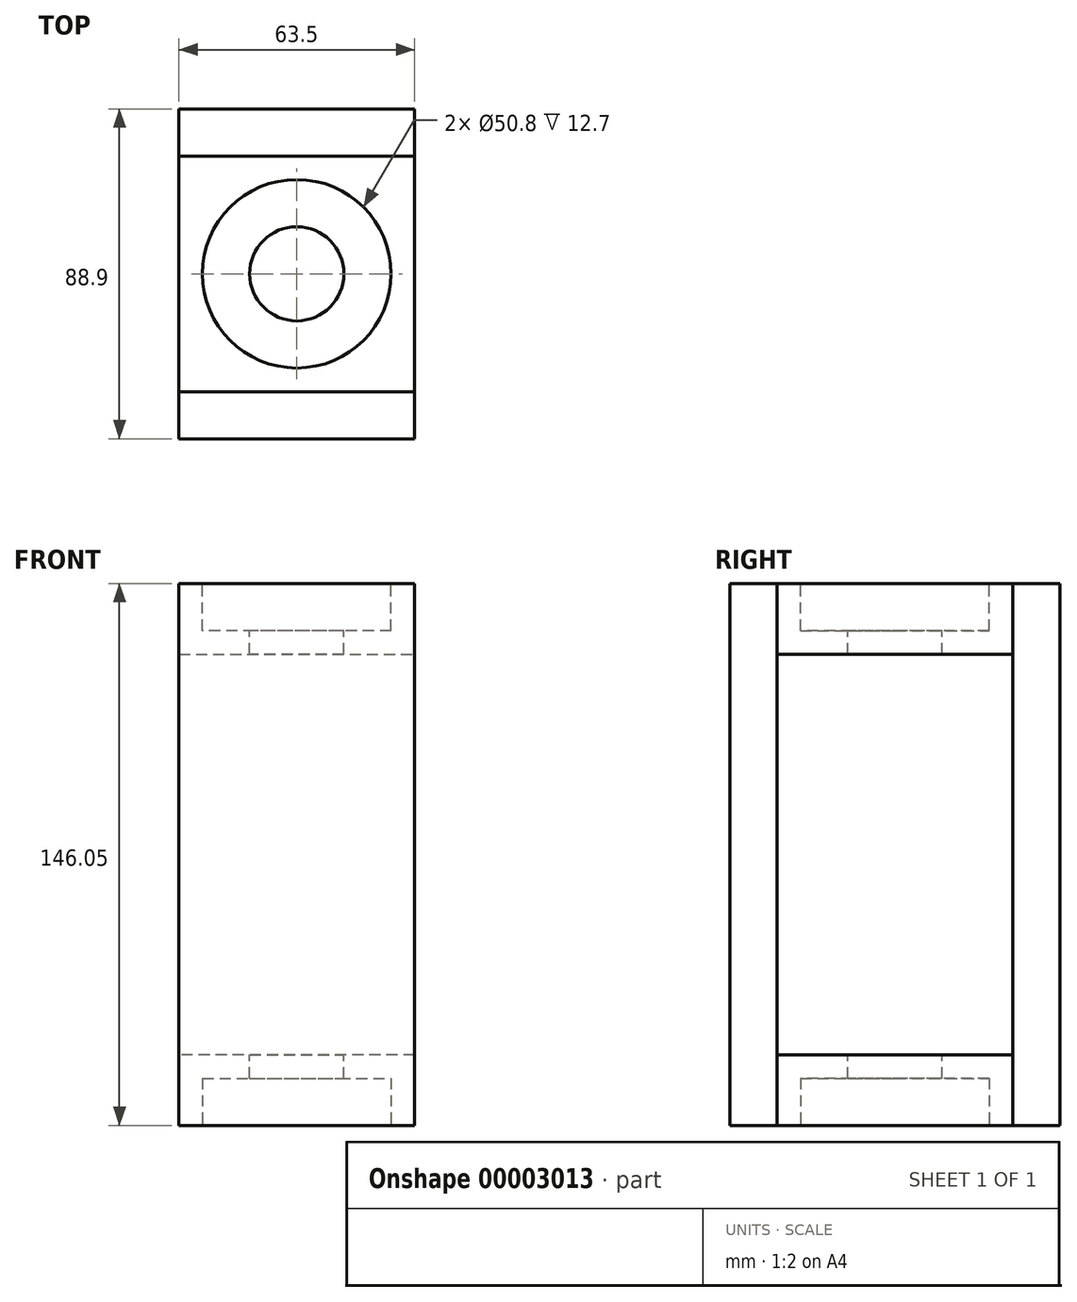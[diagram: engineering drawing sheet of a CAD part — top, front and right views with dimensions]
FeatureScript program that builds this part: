
annotation { "Feature Type Name" : "Feature", "Feature Type Description" : "" }
export const myFeature = defineFeature(function(context is Context, id is Id, definition is map)
    precondition{}
    {
        {
            var Q0;
            Q0=qCreatedBy(makeId("Top.planeOp"),FACE);
            var sketch = newSketch(context, id + "F0", { "sketchPlane" : qUnion([Q0])});
            skLineSegment(sketch, "E0.bottom", {"start": v(0, 0) * mm, "end": v(63.5, 0) * mm});
            skLineSegment(sketch, "E0.top", {"start": v(0, 63.5) * mm, "end": v(63.5, 63.5) * mm});
            skLineSegment(sketch, "E0.left", {"start": v(0, 0) * mm, "end": v(0, 63.5) * mm});
            skLineSegment(sketch, "E0.right", {"start": v(63.5, 0) * mm, "end": v(63.5, 63.5) * mm});
            skSolve(sketch);
        }
        {
            var Q0;
            Q0=makeQuery(id+"F0.imprint","IMPRINT",FACE,{"disambiguationData":[TD([[makeQuery(id+"F0.imprint","IMPRINT",EDGE,{"derivedFrom":sQuery(id+"F0.wireOp",EDGE,"E0.bottom")}),1.0]])]});
            extrude(context, id + "F1", {"entities" : qUnion([Q0]), "depth" : 19.05 * mm});
        }
        {
            var Q0;
            Q0=makeQuery(id+"F1.opExtrude","CAP_FACE",FACE,{"disambiguationData":[OSD([sQuery(id+"F0.wireOp",EDGE,"E0.bottom"),sQuery(id+"F0.wireOp",EDGE,"E0.top"),sQuery(id+"F0.wireOp",EDGE,"E0.left"),sQuery(id+"F0.wireOp",EDGE,"E0.right")])],"isStart":true});
            cPlane(context, id + "F2", {"entities" : qUnion([Q0]), "cplaneType" : CPlaneType.OFFSET, "offset" : 127 * mm, "width" : 152.4 * mm, "height" : 152.4 * mm});
        }
        {
            var Q0;
            Q0=qCreatedBy(id+"F2.planeOp",FACE);
            var sketch = newSketch(context, id + "F3", { "sketchPlane" : qUnion([Q0])});
            skLineSegment(sketch, "E1.0.0", {"start": v(0, 0) * mm, "end": v(0, -63.5) * mm});
            skLineSegment(sketch, "E1.0.1", {"start": v(0, -63.5) * mm, "end": v(63.5, -63.5) * mm});
            skLineSegment(sketch, "E1.0.2", {"start": v(63.5, -63.5) * mm, "end": v(63.5, 0) * mm});
            skLineSegment(sketch, "E1.0.3", {"start": v(63.5, 0) * mm, "end": v(0, 0) * mm});
            skSolve(sketch);
        }
        {
            var Q0;
            Q0=makeQuery(id+"F3.imprint","IMPRINT",FACE,{"disambiguationData":[TD([[makeQuery(id+"F3.imprint","IMPRINT",EDGE,{"derivedFrom":sQuery(id+"F3.wireOp",EDGE,"E1.0.0")}),1.0]])]});
            extrude(context, id + "F4", {"entities" : qUnion([Q0]), "oppositeDirection" : true, "depth" : 19.05 * mm});
        }
        {
            var Q0;
            Q0=makeQuery(id+"F1.opExtrude","CAP_FACE",FACE,{"disambiguationData":[OSD([sQuery(id+"F0.wireOp",EDGE,"E0.bottom"),sQuery(id+"F0.wireOp",EDGE,"E0.top"),sQuery(id+"F0.wireOp",EDGE,"E0.left"),sQuery(id+"F0.wireOp",EDGE,"E0.right")])],"isStart":false});
            var sketch = newSketch(context, id + "F5", { "sketchPlane" : qUnion([Q0])});
            skCircle(sketch, "E2", {"center": v(31.75, 31.75) * mm, "radius": 12.7 * mm});
            skSolve(sketch);
        }
        {
            var Q0;
            Q0=makeQuery(id+"F5.imprint","IMPRINT",FACE,{"disambiguationData":[TD([[makeQuery(id+"F5.imprint","IMPRINT",EDGE,{"derivedFrom":sQuery(id+"F5.wireOp",EDGE,"E2")}),1.0]])]});
            extrude(context, id + "F6", {"entities" : qUnion([Q0]), "operationType" : NewBodyOperationType.REMOVE, "endBound" : BoundingType.THROUGH_ALL, "oppositeDirection" : true, "depth" : 25.4 * mm});
        }
        {
            var Q0;
            Q0=makeQuery(id+"F1.opExtrude","CAP_FACE",FACE,{"disambiguationData":[OSD([sQuery(id+"F0.wireOp",EDGE,"E0.bottom"),sQuery(id+"F0.wireOp",EDGE,"E0.top"),sQuery(id+"F0.wireOp",EDGE,"E0.left"),sQuery(id+"F0.wireOp",EDGE,"E0.right")])],"isStart":false});
            var sketch = newSketch(context, id + "F7", { "sketchPlane" : qUnion([Q0])});
            skCircle(sketch, "E3", {"center": v(31.75, 31.75) * mm, "radius": 25.4 * mm});
            skSolve(sketch);
        }
        {
            var Q0;
            Q0=makeQuery(id+"F7.imprint","IMPRINT",FACE,{"disambiguationData":[TD([[makeQuery(id+"F7.imprint","IMPRINT",EDGE,{"derivedFrom":sQuery(id+"F7.wireOp",EDGE,"E3")}),1.0]])]});
            extrude(context, id + "F8", {"entities" : qUnion([Q0]), "operationType" : NewBodyOperationType.REMOVE, "oppositeDirection" : true, "depth" : 12.7 * mm});
        }
        {
            var Q0;
            Q0=makeQuery(id+"F4.opExtrude","CAP_FACE",FACE,{"disambiguationData":[OSD([sQuery(id+"F3.wireOp",EDGE,"E1.0.0"),sQuery(id+"F3.wireOp",EDGE,"E1.0.1"),sQuery(id+"F3.wireOp",EDGE,"E1.0.2"),sQuery(id+"F3.wireOp",EDGE,"E1.0.3")])],"isStart":true});
            var sketch = newSketch(context, id + "F9", { "sketchPlane" : qUnion([Q0])});
            skCircle(sketch, "E4", {"center": v(31.75, -31.75) * mm, "radius": 25.4 * mm});
            skSolve(sketch);
        }
        {
            var Q0;
            Q0=makeQuery(id+"F9.imprint","IMPRINT",FACE,{"disambiguationData":[TD([[makeQuery(id+"F9.imprint","IMPRINT",EDGE,{"derivedFrom":sQuery(id+"F9.wireOp",EDGE,"E4")}),1.0]])]});
            extrude(context, id + "F10", {"entities" : qUnion([Q0]), "operationType" : NewBodyOperationType.REMOVE, "oppositeDirection" : true, "depth" : 12.7 * mm});
        }
        {
            var Q0;
            Q0=makeQuery(id+"F1.opExtrude","SWEPT_FACE",FACE,{"disambiguationData":[OSD([sQuery(id+"F0.wireOp",EDGE,"E0.bottom")])]});
            var sketch = newSketch(context, id + "F11", { "sketchPlane" : qUnion([Q0])});
            skPoint(sketch, "E5.0", {"position": v(63.5, -127) * mm});
            skLineSegment(sketch, "E6.bottom", {"start": v(0, 19.05) * mm, "end": v(63.5, 19.05) * mm});
            skLineSegment(sketch, "E6.top", {"start": v(0, -127) * mm, "end": v(63.5, -127) * mm});
            skLineSegment(sketch, "E6.left", {"start": v(0, 19.05) * mm, "end": v(0, -127) * mm});
            skLineSegment(sketch, "E6.right", {"start": v(63.5, 19.05) * mm, "end": v(63.5, -127) * mm});
            skSolve(sketch);
        }
        {
            var Q0;
            {var subQ2=sQuery(id+"F11.wireOp",EDGE,"E6.bottom");Q0=makeQuery(id+"F11.imprint","IMPRINT",FACE,{"disambiguationData":[TD([[makeQuery(id+"F11.imprint","IMPRINT",EDGE,{"derivedFrom":subQ2}),-1.0]])]});}
            var Q1;
            {var subQ2=sQuery(id+"F11.wireOp",EDGE,"E6.top");Q1=makeQuery(id+"F11.imprint","IMPRINT",FACE,{"disambiguationData":[TD([[makeQuery(id+"F11.imprint","IMPRINT",EDGE,{"derivedFrom":subQ2}),1.0]])]});}
            extrude(context, id + "F12", {"entities" : qUnion([Q0, Q1]), "depth" : 12.7 * mm});
        }
        {
            var Q0;
            Q0=makeQuery(id+"F1.opExtrude","SWEPT_FACE",FACE,{"disambiguationData":[OSD([sQuery(id+"F0.wireOp",EDGE,"E0.top")])]});
            var sketch = newSketch(context, id + "F13", { "sketchPlane" : qUnion([Q0])});
            skLineSegment(sketch, "E7.0.0", {"start": v(0, 19.05) * mm, "end": v(0, -127) * mm});
            skLineSegment(sketch, "E7.0.1", {"start": v(0, -127) * mm, "end": v(-63.5, -127) * mm});
            skLineSegment(sketch, "E7.0.2", {"start": v(-63.5, -127) * mm, "end": v(-63.5, 19.05) * mm});
            skLineSegment(sketch, "E7.0.3", {"start": v(-63.5, 19.05) * mm, "end": v(0, 19.05) * mm});
            skSolve(sketch);
        }
        {
            var Q0;
            {var subQ2=sQuery(id+"F13.wireOp",EDGE,"E7.0.1");Q0=makeQuery(id+"F13.imprint","IMPRINT",FACE,{"disambiguationData":[TD([[makeQuery(id+"F13.imprint","IMPRINT",EDGE,{"derivedFrom":subQ2}),-1.0]])]});}
            var Q1;
            {var subQ1=sQuery(id+"F13.wireOp",EDGE,"E7.0.3");Q1=makeQuery(id+"F13.imprint","IMPRINT",FACE,{"disambiguationData":[TD([[makeQuery(id+"F13.imprint","IMPRINT",EDGE,{"derivedFrom":subQ1}),1.0]])]});}
            extrude(context, id + "F14", {"entities" : qUnion([Q0, Q1]), "depth" : 12.7 * mm});
        }
    });
